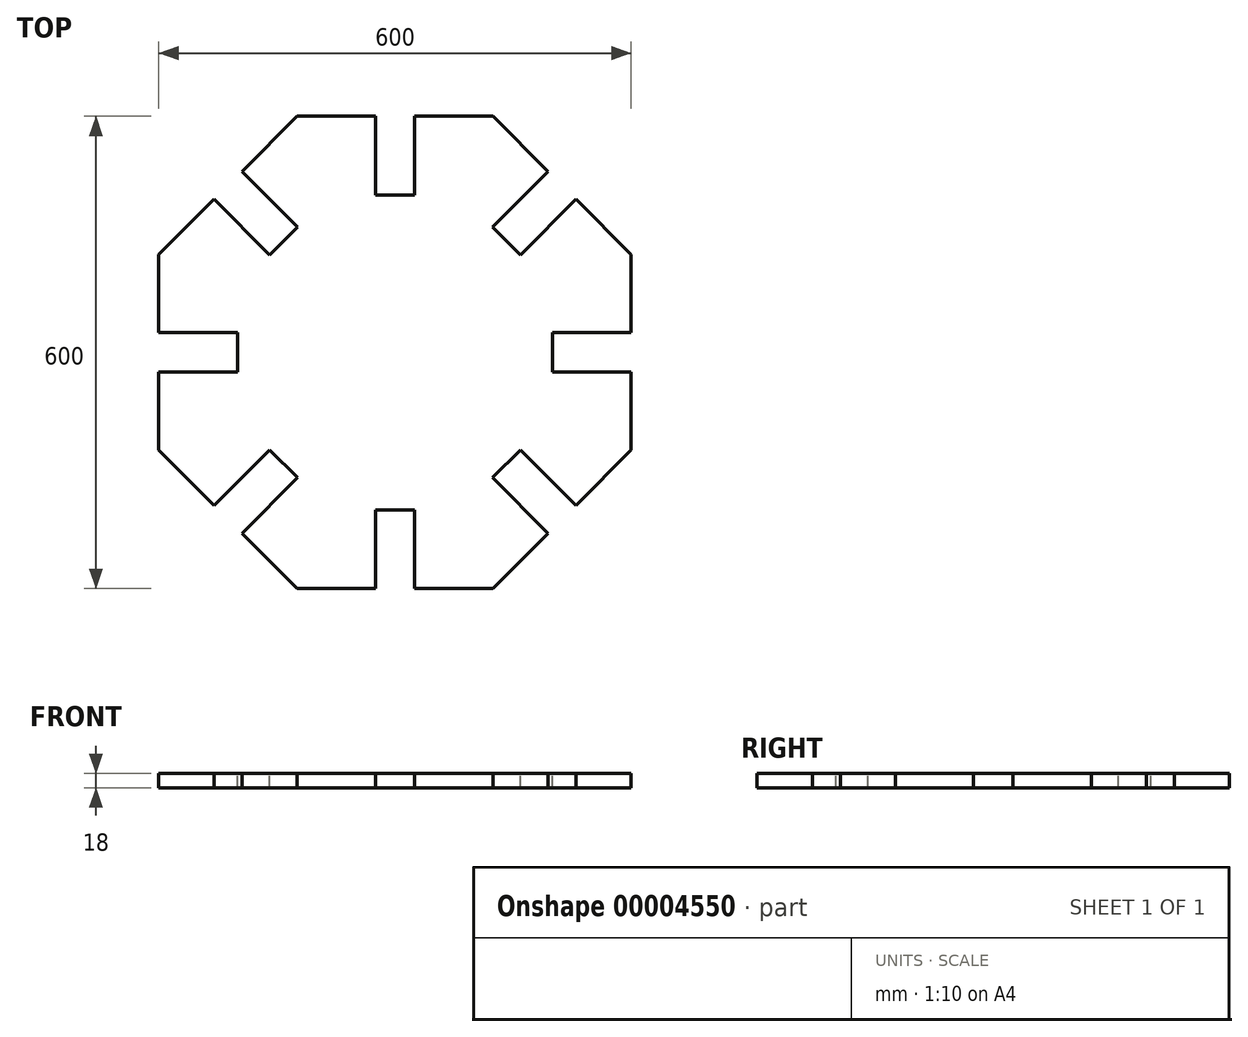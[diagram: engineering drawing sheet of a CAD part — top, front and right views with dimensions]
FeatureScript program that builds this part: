
annotation { "Feature Type Name" : "Feature", "Feature Type Description" : "" }
export const myFeature = defineFeature(function(context is Context, id is Id, definition is map)
    precondition{}
    {
        {
            var Q0;
            Q0=qCreatedBy(makeId("Top.planeOp"),FACE);
            var sketch = newSketch(context, id + "F0", { "sketchPlane" : qUnion([Q0])});
            skCircle(sketch, "E0", {"center": v(-365.51, 26.05) * mm, "radius": 300 * mm, "construction": true});
            skLineSegment(sketch, "E1.0", {"start": v(-665.51, -98.22) * mm, "end": v(-665.51, 150.31) * mm});
            skLineSegment(sketch, "E1.1", {"start": v(-665.51, 150.31) * mm, "end": v(-489.78, 326.05) * mm});
            skLineSegment(sketch, "E1.2", {"start": v(-489.78, 326.05) * mm, "end": v(-241.25, 326.05) * mm});
            skLineSegment(sketch, "E1.3", {"start": v(-241.25, 326.05) * mm, "end": v(-65.51, 150.31) * mm});
            skLineSegment(sketch, "E1.4", {"start": v(-65.51, 150.31) * mm, "end": v(-65.51, -98.22) * mm});
            skLineSegment(sketch, "E1.5", {"start": v(-65.51, -98.22) * mm, "end": v(-241.25, -273.95) * mm});
            skLineSegment(sketch, "E1.6", {"start": v(-241.25, -273.95) * mm, "end": v(-489.78, -273.95) * mm});
            skLineSegment(sketch, "E1.7", {"start": v(-489.78, -273.95) * mm, "end": v(-665.51, -98.22) * mm});
            skPoint(sketch, "E1.0.midPoint", {"position": v(-665.51, 26.05) * mm});
            skSolve(sketch);
        }
        {
            var Q0;
            Q0=makeQuery(id+"F0.imprint","IMPRINT",FACE,{"disambiguationData":[TD([[makeQuery(id+"F0.imprint","IMPRINT",EDGE,{"derivedFrom":sQuery(id+"F0.wireOp",EDGE,"E1.0")}),-1.0]])]});
            extrude(context, id + "F1", {"entities" : qUnion([Q0]), "depth" : 18 * mm});
        }
        {
            var Q0;
            Q0=makeQuery(id+"F1.opExtrude","CAP_FACE",FACE,{"disambiguationData":[OSD([sQuery(id+"F0.wireOp",EDGE,"E1.0"),sQuery(id+"F0.wireOp",EDGE,"E1.1"),sQuery(id+"F0.wireOp",EDGE,"E1.2"),sQuery(id+"F0.wireOp",EDGE,"E1.3"),sQuery(id+"F0.wireOp",EDGE,"E1.4"),sQuery(id+"F0.wireOp",EDGE,"E1.5"),sQuery(id+"F0.wireOp",EDGE,"E1.6"),sQuery(id+"F0.wireOp",EDGE,"E1.7")])],"isStart":false});
            var sketch = newSketch(context, id + "F2", { "sketchPlane" : qUnion([Q0])});
            skLineSegment(sketch, "E2", {"start": v(-365.51, 326.05) * mm, "end": v(-365.51, -273.95) * mm, "construction": true});
            skLineSegment(sketch, "E3.rect.bottom", {"start": v(-340.51, -283.95) * mm, "end": v(-390.51, -283.95) * mm});
            skLineSegment(sketch, "E3.rect.top", {"start": v(-340.51, -173.95) * mm, "end": v(-390.51, -173.95) * mm});
            skLineSegment(sketch, "E3.rect.left", {"start": v(-340.51, -283.95) * mm, "end": v(-340.51, -173.95) * mm});
            skLineSegment(sketch, "E3.rect.right", {"start": v(-390.51, -283.95) * mm, "end": v(-390.51, -173.95) * mm});
            skPoint(sketch, "E3.rect.middle", {"position": v(-365.51, -228.95) * mm});
            skPoint(sketch, "E4", {"position": v(-365.51, 26.05) * mm});
            skLineSegment(sketch, "E5.1.0", {"start": v(-206.41, -97.7) * mm, "end": v(-241.77, -133.05) * mm});
            skLineSegment(sketch, "E5.1.1", {"start": v(-128.63, -175.48) * mm, "end": v(-163.99, -210.83) * mm});
            skLineSegment(sketch, "E5.1.2", {"start": v(-163.99, -210.83) * mm, "end": v(-241.77, -133.05) * mm});
            skPoint(sketch, "E5.1.3", {"position": v(-185.2, -154.26) * mm});
            skLineSegment(sketch, "E5.1.4", {"start": v(-128.63, -175.48) * mm, "end": v(-206.41, -97.7) * mm});
            skLineSegment(sketch, "E5.2.0", {"start": v(-165.51, 51.05) * mm, "end": v(-165.51, 1.05) * mm});
            skLineSegment(sketch, "E5.2.1", {"start": v(-55.51, 51.05) * mm, "end": v(-55.51, 1.05) * mm});
            skLineSegment(sketch, "E5.2.2", {"start": v(-55.51, 1.05) * mm, "end": v(-165.51, 1.05) * mm});
            skPoint(sketch, "E5.2.3", {"position": v(-110.51, 26.05) * mm});
            skLineSegment(sketch, "E5.2.4", {"start": v(-55.51, 51.05) * mm, "end": v(-165.51, 51.05) * mm});
            skLineSegment(sketch, "E5.3.0", {"start": v(-241.77, 185.15) * mm, "end": v(-206.41, 149.8) * mm});
            skLineSegment(sketch, "E5.3.1", {"start": v(-163.99, 262.93) * mm, "end": v(-128.63, 227.57) * mm});
            skLineSegment(sketch, "E5.3.2", {"start": v(-128.63, 227.57) * mm, "end": v(-206.41, 149.8) * mm});
            skPoint(sketch, "E5.3.3", {"position": v(-185.2, 206.36) * mm});
            skLineSegment(sketch, "E5.3.4", {"start": v(-163.99, 262.93) * mm, "end": v(-241.77, 185.15) * mm});
            skLineSegment(sketch, "E5.4.0", {"start": v(-390.51, 226.05) * mm, "end": v(-340.51, 226.05) * mm});
            skLineSegment(sketch, "E5.4.1", {"start": v(-390.51, 336.05) * mm, "end": v(-340.51, 336.05) * mm});
            skLineSegment(sketch, "E5.4.2", {"start": v(-340.51, 336.05) * mm, "end": v(-340.51, 226.05) * mm});
            skPoint(sketch, "E5.4.3", {"position": v(-365.51, 281.05) * mm});
            skLineSegment(sketch, "E5.4.4", {"start": v(-390.51, 336.05) * mm, "end": v(-390.51, 226.05) * mm});
            skLineSegment(sketch, "E5.5.0", {"start": v(-524.61, 149.8) * mm, "end": v(-489.26, 185.15) * mm});
            skLineSegment(sketch, "E5.5.1", {"start": v(-602.4, 227.57) * mm, "end": v(-567.04, 262.93) * mm});
            skLineSegment(sketch, "E5.5.2", {"start": v(-567.04, 262.93) * mm, "end": v(-489.26, 185.15) * mm});
            skPoint(sketch, "E5.5.3", {"position": v(-545.83, 206.36) * mm});
            skLineSegment(sketch, "E5.5.4", {"start": v(-602.4, 227.57) * mm, "end": v(-524.61, 149.8) * mm});
            skLineSegment(sketch, "E5.6.0", {"start": v(-565.51, 1.05) * mm, "end": v(-565.51, 51.05) * mm});
            skLineSegment(sketch, "E5.6.1", {"start": v(-675.51, 1.05) * mm, "end": v(-675.51, 51.05) * mm});
            skLineSegment(sketch, "E5.6.2", {"start": v(-675.51, 51.05) * mm, "end": v(-565.51, 51.05) * mm});
            skPoint(sketch, "E5.6.3", {"position": v(-620.51, 26.05) * mm});
            skLineSegment(sketch, "E5.6.4", {"start": v(-675.51, 1.05) * mm, "end": v(-565.51, 1.05) * mm});
            skLineSegment(sketch, "E5.7.0", {"start": v(-489.26, -133.05) * mm, "end": v(-524.61, -97.7) * mm});
            skLineSegment(sketch, "E5.7.1", {"start": v(-567.04, -210.83) * mm, "end": v(-602.4, -175.48) * mm});
            skLineSegment(sketch, "E5.7.2", {"start": v(-602.4, -175.48) * mm, "end": v(-524.61, -97.7) * mm});
            skPoint(sketch, "E5.7.3", {"position": v(-545.83, -154.26) * mm});
            skLineSegment(sketch, "E5.7.4", {"start": v(-567.04, -210.83) * mm, "end": v(-489.26, -133.05) * mm});
            skSolve(sketch);
        }
        {
            var Q0;
            {var subQ6=sQuery(id+"F2.wireOp",EDGE,"E3.rect.bottom");var subQ13=sQuery(id+"F2.wireOp",EDGE,"E5.1.1");var subQ20=sQuery(id+"F2.wireOp",EDGE,"E5.2.1");var subQ27=sQuery(id+"F2.wireOp",EDGE,"E5.3.1");var subQ31=sQuery(id+"F2.wireOp",EDGE,"E5.4.1");var subQ41=sQuery(id+"F2.wireOp",EDGE,"E5.5.1");var subQ48=sQuery(id+"F2.wireOp",EDGE,"E5.6.1");var subQ55=sQuery(id+"F2.wireOp",EDGE,"E5.7.1");var subQ56=sQuery(id+"F2.wireOp",EDGE,"E3.rect.top");var subQ57=sQuery(id+"F2.wireOp",EDGE,"E5.1.0");var subQ58=sQuery(id+"F2.wireOp",EDGE,"E5.2.0");var subQ59=sQuery(id+"F2.wireOp",EDGE,"E5.3.0");var subQ60=sQuery(id+"F2.wireOp",EDGE,"E5.4.0");var subQ61=sQuery(id+"F2.wireOp",EDGE,"E5.5.0");var subQ62=sQuery(id+"F2.wireOp",EDGE,"E5.6.0");var subQ63=sQuery(id+"F2.wireOp",EDGE,"E5.7.0");Q0=qUnion([makeQuery(id+"F2.imprint","IMPRINT",FACE,{"disambiguationData":[TD([[makeQuery(id+"F2.imprint","IMPRINT",EDGE,{"derivedFrom":subQ6}),-1.0]])]}),makeQuery(id+"F2.imprint","IMPRINT",FACE,{"disambiguationData":[TD([[makeQuery(id+"F2.imprint","IMPRINT",EDGE,{"derivedFrom":subQ13}),-1.0]])]}),makeQuery(id+"F2.imprint","IMPRINT",FACE,{"disambiguationData":[TD([[makeQuery(id+"F2.imprint","IMPRINT",EDGE,{"derivedFrom":subQ20}),-1.0]])]}),makeQuery(id+"F2.imprint","IMPRINT",FACE,{"disambiguationData":[TD([[makeQuery(id+"F2.imprint","IMPRINT",EDGE,{"derivedFrom":subQ27}),-1.0]])]}),makeQuery(id+"F2.imprint","IMPRINT",FACE,{"disambiguationData":[TD([[makeQuery(id+"F2.imprint","IMPRINT",EDGE,{"derivedFrom":subQ31}),-1.0]])]}),makeQuery(id+"F2.imprint","IMPRINT",FACE,{"disambiguationData":[TD([[makeQuery(id+"F2.imprint","IMPRINT",EDGE,{"derivedFrom":subQ41}),-1.0]])]}),makeQuery(id+"F2.imprint","IMPRINT",FACE,{"disambiguationData":[TD([[makeQuery(id+"F2.imprint","IMPRINT",EDGE,{"derivedFrom":subQ48}),-1.0]])]}),makeQuery(id+"F2.imprint","IMPRINT",FACE,{"disambiguationData":[TD([[makeQuery(id+"F2.imprint","IMPRINT",EDGE,{"derivedFrom":subQ55}),-1.0]])]}),makeQuery(id+"F2.imprint","IMPRINT",FACE,{"disambiguationData":[TD([[makeQuery(id+"F2.imprint","IMPRINT",EDGE,{"derivedFrom":subQ56}),1.0]])]}),makeQuery(id+"F2.imprint","IMPRINT",FACE,{"disambiguationData":[TD([[makeQuery(id+"F2.imprint","IMPRINT",EDGE,{"derivedFrom":subQ57}),1.0]])]}),makeQuery(id+"F2.imprint","IMPRINT",FACE,{"disambiguationData":[TD([[makeQuery(id+"F2.imprint","IMPRINT",EDGE,{"derivedFrom":subQ58}),1.0]])]}),makeQuery(id+"F2.imprint","IMPRINT",FACE,{"disambiguationData":[TD([[makeQuery(id+"F2.imprint","IMPRINT",EDGE,{"derivedFrom":subQ59}),1.0]])]}),makeQuery(id+"F2.imprint","IMPRINT",FACE,{"disambiguationData":[TD([[makeQuery(id+"F2.imprint","IMPRINT",EDGE,{"derivedFrom":subQ60}),1.0]])]}),makeQuery(id+"F2.imprint","IMPRINT",FACE,{"disambiguationData":[TD([[makeQuery(id+"F2.imprint","IMPRINT",EDGE,{"derivedFrom":subQ61}),1.0]])]}),makeQuery(id+"F2.imprint","IMPRINT",FACE,{"disambiguationData":[TD([[makeQuery(id+"F2.imprint","IMPRINT",EDGE,{"derivedFrom":subQ62}),1.0]])]}),makeQuery(id+"F2.imprint","IMPRINT",FACE,{"disambiguationData":[TD([[makeQuery(id+"F2.imprint","IMPRINT",EDGE,{"derivedFrom":subQ63}),1.0]])]})]);}
            extrude(context, id + "F3", {"entities" : qUnion([Q0]), "operationType" : NewBodyOperationType.REMOVE, "oppositeDirection" : true, "depth" : 25 * mm});
        }
    });
